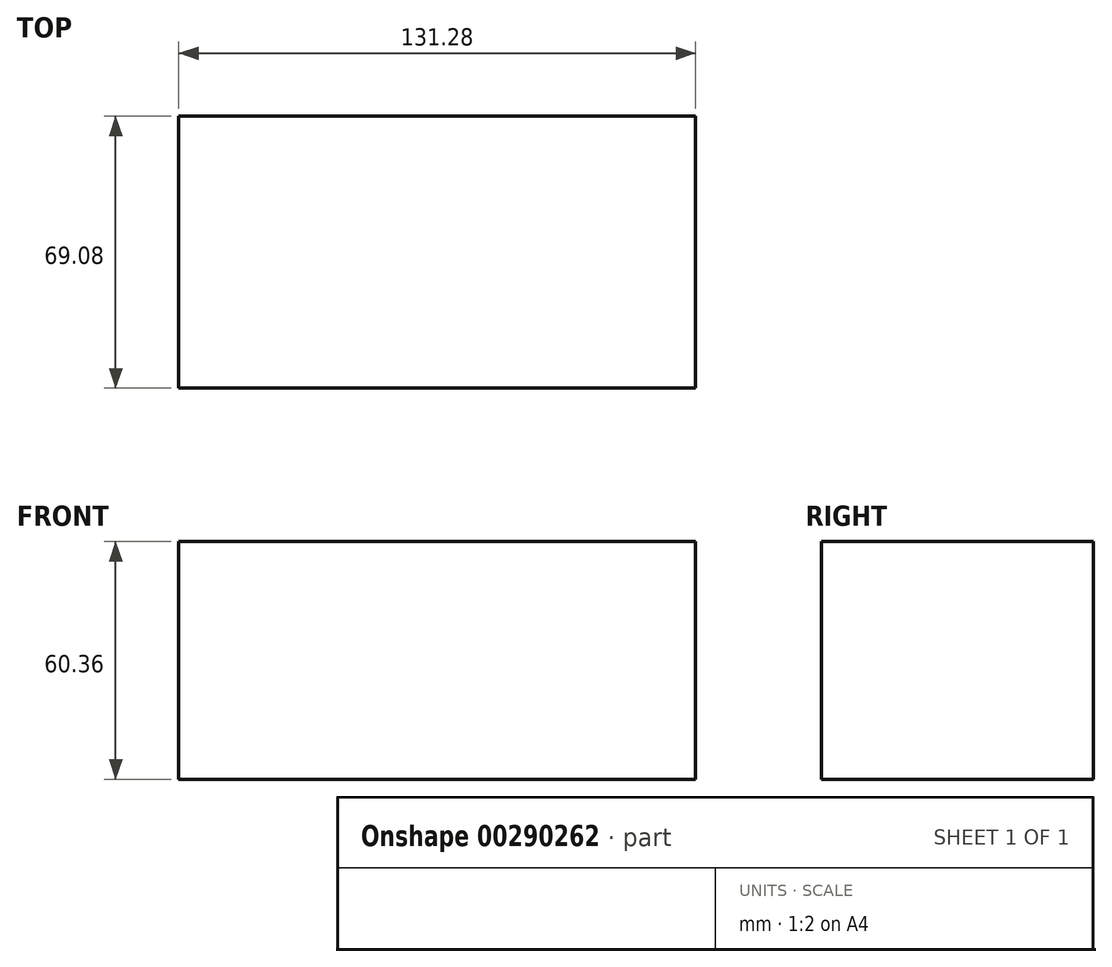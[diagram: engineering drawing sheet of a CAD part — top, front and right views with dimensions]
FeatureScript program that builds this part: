
annotation { "Feature Type Name" : "Feature", "Feature Type Description" : "" }
export const myFeature = defineFeature(function(context is Context, id is Id, definition is map)
    precondition{}
    {
        {
            var Q0;
            Q0=qCreatedBy(makeId("Front.planeOp"),FACE);
            var sketch = newSketch(context, id + "F0", { "sketchPlane" : qUnion([Q0])});
            skLineSegment(sketch, "E0.bottom", {"start": v(65.64, -30.18) * mm, "end": v(-65.64, -30.18) * mm});
            skLineSegment(sketch, "E0.top", {"start": v(65.64, 30.18) * mm, "end": v(-65.64, 30.18) * mm});
            skLineSegment(sketch, "E0.left", {"start": v(65.64, -30.18) * mm, "end": v(65.64, 30.18) * mm});
            skLineSegment(sketch, "E0.right", {"start": v(-65.64, -30.18) * mm, "end": v(-65.64, 30.18) * mm});
            skPoint(sketch, "E0.middle", {"position": v(0, 0) * mm});
            skSolve(sketch);
        }
        {
            var Q0;
            Q0 = qSketchRegion(id + "F0", true);
            extrude(context, id + "F1", {"entities" : qUnion([Q0]), "endBound" : BoundingType.SYMMETRIC, "depth" : 69.1 * mm});
        }
    });
